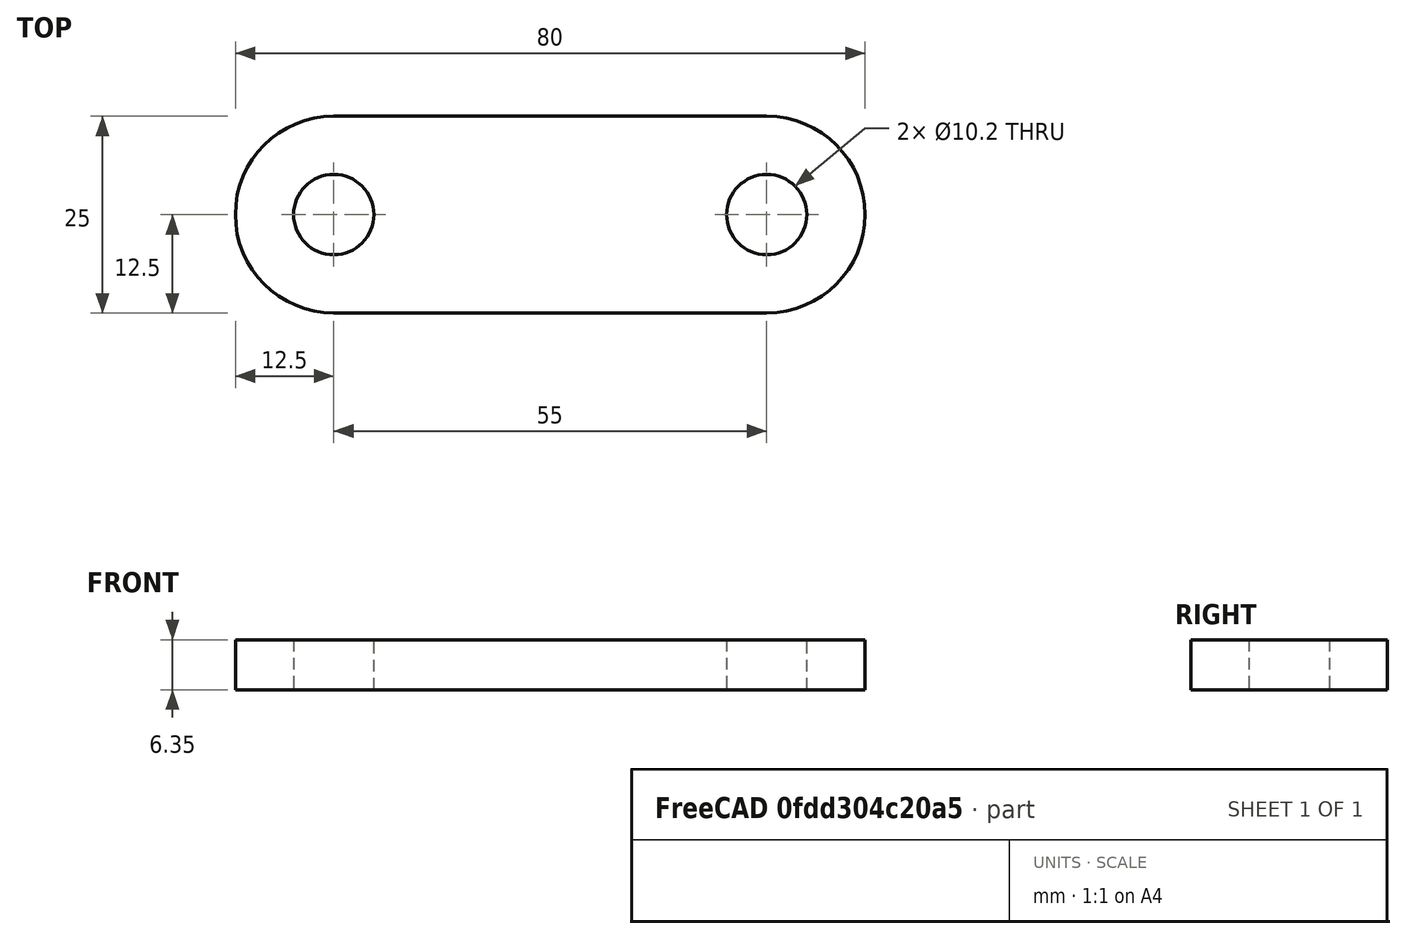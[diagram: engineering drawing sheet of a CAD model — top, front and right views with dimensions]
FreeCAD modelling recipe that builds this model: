
FCSTD DOCUMENT  (FreeCAD 0.21R33694 (Git))
Label: smart shunt link
License: All rights reserved
LicenseURL: http://en.wikipedia.org/wiki/All_rights_reserved
objects: Sketcher::SketchObject×1, PartDesign::Pad×1, PartDesign::Body×1, TechDraw::DrawSVGTemplate×1, TechDraw::DrawPage×1
note: 4 computed .brp shape members not serialized (recipe doc carries the construction recipe); baked Part::Feature solids carry a one-line shape summary decoded from their .brp

FEATURE [Sketcher::SketchObject] Sketch
  FullyConstrained = true
  MapMode = 5
  Support = -> [XY_Plane]
  sketch-geometry (6):
    g0: ArcOfCircle CenterX=-27.5 CenterY=0 CenterZ=0 NormalX=0 NormalY=0 NormalZ=1 AngleXU=0 Radius=12.5 StartAngle=1.5708 EndAngle=4.71239
    g1: ArcOfCircle CenterX=27.5 CenterY=0 CenterZ=0 NormalX=0 NormalY=0 NormalZ=1 AngleXU=0 Radius=12.5 StartAngle=4.71239 EndAngle=7.85398
    g2: LineSegment StartX=-27.5 StartY=12.5 StartZ=0 EndX=27.5 EndY=12.5 EndZ=0
    g3: LineSegment StartX=27.5 StartY=-12.5 StartZ=0 EndX=-27.5 EndY=-12.5 EndZ=0
    g4: Circle CenterX=-27.5 CenterY=0 CenterZ=0 NormalX=0 NormalY=0 NormalZ=1 AngleXU=0 Radius=5.1
    g5: Circle CenterX=27.5 CenterY=0 CenterZ=0 NormalX=0 NormalY=0 NormalZ=1 AngleXU=0 Radius=5.1
  constraints (16):
    c: PointOnObject(g0,g-1)
    c: PointOnObject(g1,g-1)
    c: Diameter(g0) = 25
    c: Diameter(g1) = 25
    c: Horizontal(g2)
    c: Horizontal(g3)
    c: DistanceX(g2,g2) = 55
    c: Coincident(g0,g3)
    c: Tangent(g0,g2) = 1.5708
    c: Coincident(g1,g2)
    c: Tangent(g1,g3) = 1.5708
    c: DistanceX(g0,g-1) = 27.5
    c: Coincident(g4,g0)
    c: Coincident(g5,g1)
    c: Diameter(g4) = 10.2
    c: Diameter(g5) = 10.2
FEATURE [PartDesign::Pad] Pad
  Direction = (0,0,1)
  Length = 6.35
  Length2 = 10
  Profile = -> Sketch
  ReferenceAxis = -> Sketch [N_Axis]
  Type = 0
FEATURE [PartDesign::Body] Body
  Group = -> [Sketch,Pad]
  Origin = -> Origin
  Tip = -> Pad
FEATURE [TechDraw::DrawSVGTemplate] Template
  EditableTexts = Designed_by_Name=Designed by Name; Drawing_number=Drawing number; FC-Date=Date; FC-SC=Scale; FC-SH=Sheet; FC-Title=Title; Subtitle=Subtitle; Weight=Weight
  Height = 210
  Orientation = 1
  Template = /Applications/FreeCAD.app/Contents/Resources/share/Mod/TechDraw/Templates/A4_LandscapeTD.svg
  Width = 297
FEATURE [TechDraw::DrawPage] Page
  KeepUpdated = true
  NextBalloonIndex = 1
  ProjectionType = 0
  Template = -> Template
